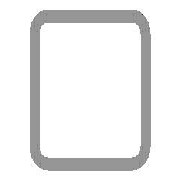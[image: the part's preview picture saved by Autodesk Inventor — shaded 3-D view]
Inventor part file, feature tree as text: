
AUTODESK INVENTOR PART (.ipt)
format: ipt  version: 2022.1 (Build 261234000, 234)  size: 134,144 bytes
history: native  units: mm (DEFAULTED — no unit token found)
features: other x4, sketch x3, extrude x1, plane x1
ambient origin geometry x8: Origin, YZ Plane, XZ Plane, XY Plane, X Axis, Y Axis, Z Axis, Center Point
bodies: Solid1 (feature_tree)
feature tree (9):
  parser-record x1  (decoder bookkeeping rows leaked as tree rows — omitted from the tree; the rows remain in map.json)
  other  "Driven Length"
  other  "Plano inicial"
  other  "Plano final"
  extrude  "Cuerpo"  TaperAngle=0.0deg  [1 undecoded]
  sketch  "Boceto"  dims[d10=40.0mm d11=40.0mm d12=5.0mm d13=-0.0mm d14=575.0mm d15=20.0mm d16=20.0mm d17=90.0deg d18=575.0mm]
  sketch  "Sketch3"  dims[d3=575.0mm d4=0.0mm]
  plane  "Work Plane3"
  sketch  "Sketch4"  dims[d7=7.5mm]
note: 1 required parameter value undecoded (feature->parameter linkage not recoverable at this tier; creation-order binding heuristic only, values carry confidence <= 0.55)
